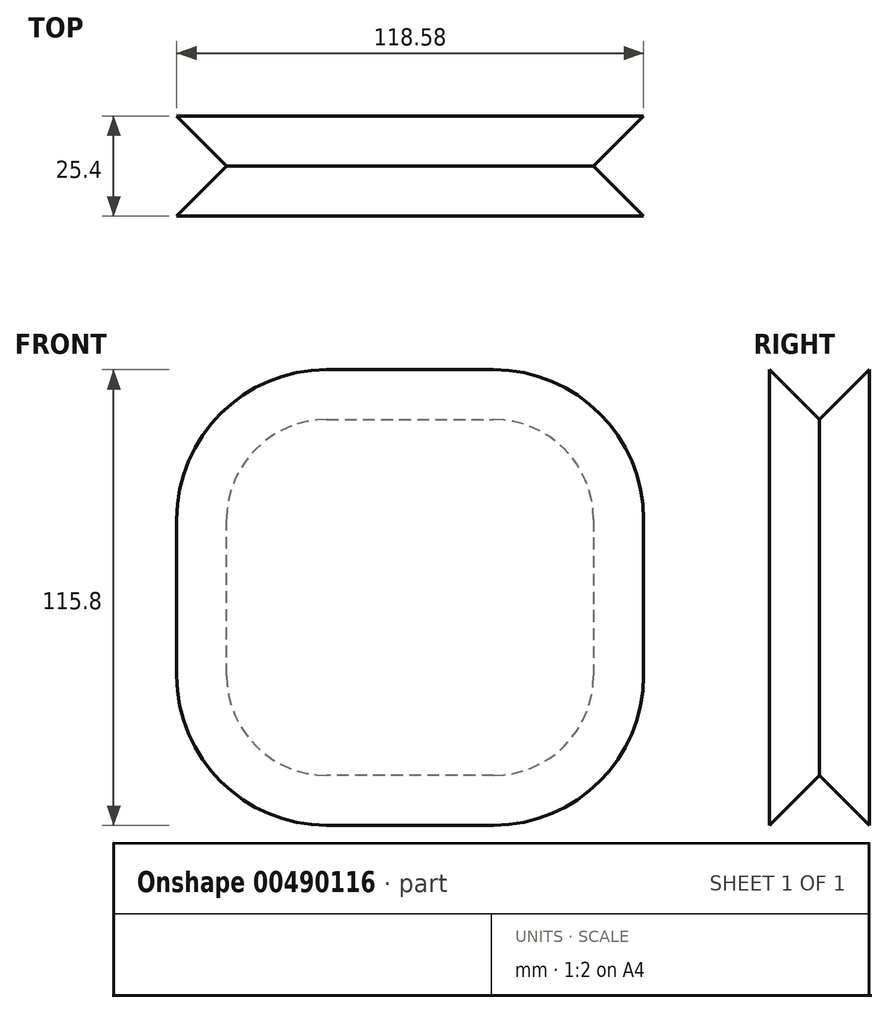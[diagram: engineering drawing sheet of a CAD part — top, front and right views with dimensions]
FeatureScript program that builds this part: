
annotation { "Feature Type Name" : "Feature", "Feature Type Description" : "" }
export const myFeature = defineFeature(function(context is Context, id is Id, definition is map)
    precondition{}
    {
        {
            var Q0;
            Q0=qCreatedBy(makeId("Front.planeOp"),FACE);
            var sketch = newSketch(context, id + "F0", { "sketchPlane" : qUnion([Q0])});
            skLineSegment(sketch, "E0.bottom", {"start": v(-21.2, 45.2) * mm, "end": v(21.2, 45.2) * mm});
            skLineSegment(sketch, "E0.top", {"start": v(-21.2, -45.2) * mm, "end": v(21.2, -45.2) * mm});
            skLineSegment(sketch, "E0.left", {"start": v(-46.6, 19.8) * mm, "end": v(-46.6, -19.8) * mm});
            skLineSegment(sketch, "E0.right", {"start": v(46.6, 19.8) * mm, "end": v(46.6, -19.8) * mm});
            skPoint(sketch, "E0.middle", {"position": v(0, 0) * mm});
            skPoint(sketch, "E1.visualSharp", {"position": v(-46.6, 45.2) * mm});
            skArc(sketch, "E1.filletArc", {"start": v(-21.2, 45.2) * mm, "mid": v(-39.15, 37.76) * mm, "end": v(-46.6, 19.8) * mm});
            skPoint(sketch, "E2.visualSharp", {"position": v(46.6, 45.2) * mm});
            skArc(sketch, "E2.filletArc", {"start": v(46.6, 19.8) * mm, "mid": v(39.15, 37.76) * mm, "end": v(21.2, 45.2) * mm});
            skPoint(sketch, "E3.visualSharp", {"position": v(46.6, -45.2) * mm});
            skArc(sketch, "E3.filletArc", {"start": v(21.2, -45.2) * mm, "mid": v(39.15, -37.76) * mm, "end": v(46.6, -19.8) * mm});
            skPoint(sketch, "E4.visualSharp", {"position": v(-46.6, -45.2) * mm});
            skArc(sketch, "E4.filletArc", {"start": v(-46.6, -19.8) * mm, "mid": v(-39.15, -37.76) * mm, "end": v(-21.2, -45.2) * mm});
            skSolve(sketch);
        }
        {
            var Q0;
            Q0=makeQuery(id+"F0.imprint","IMPRINT",FACE,{"disambiguationData":[TD([[makeQuery(id+"F0.imprint","IMPRINT",EDGE,{"derivedFrom":sQuery(id+"F0.wireOp",EDGE,"E0.bottom")}),-1.0]])]});
            extrude(context, id + "F1", {"entities" : qUnion([Q0]), "endBound" : BoundingType.SYMMETRIC, "depth" : 25.4 * mm, "hasDraft" : true, "draftAngle" : 45 * degree});
        }
    });
